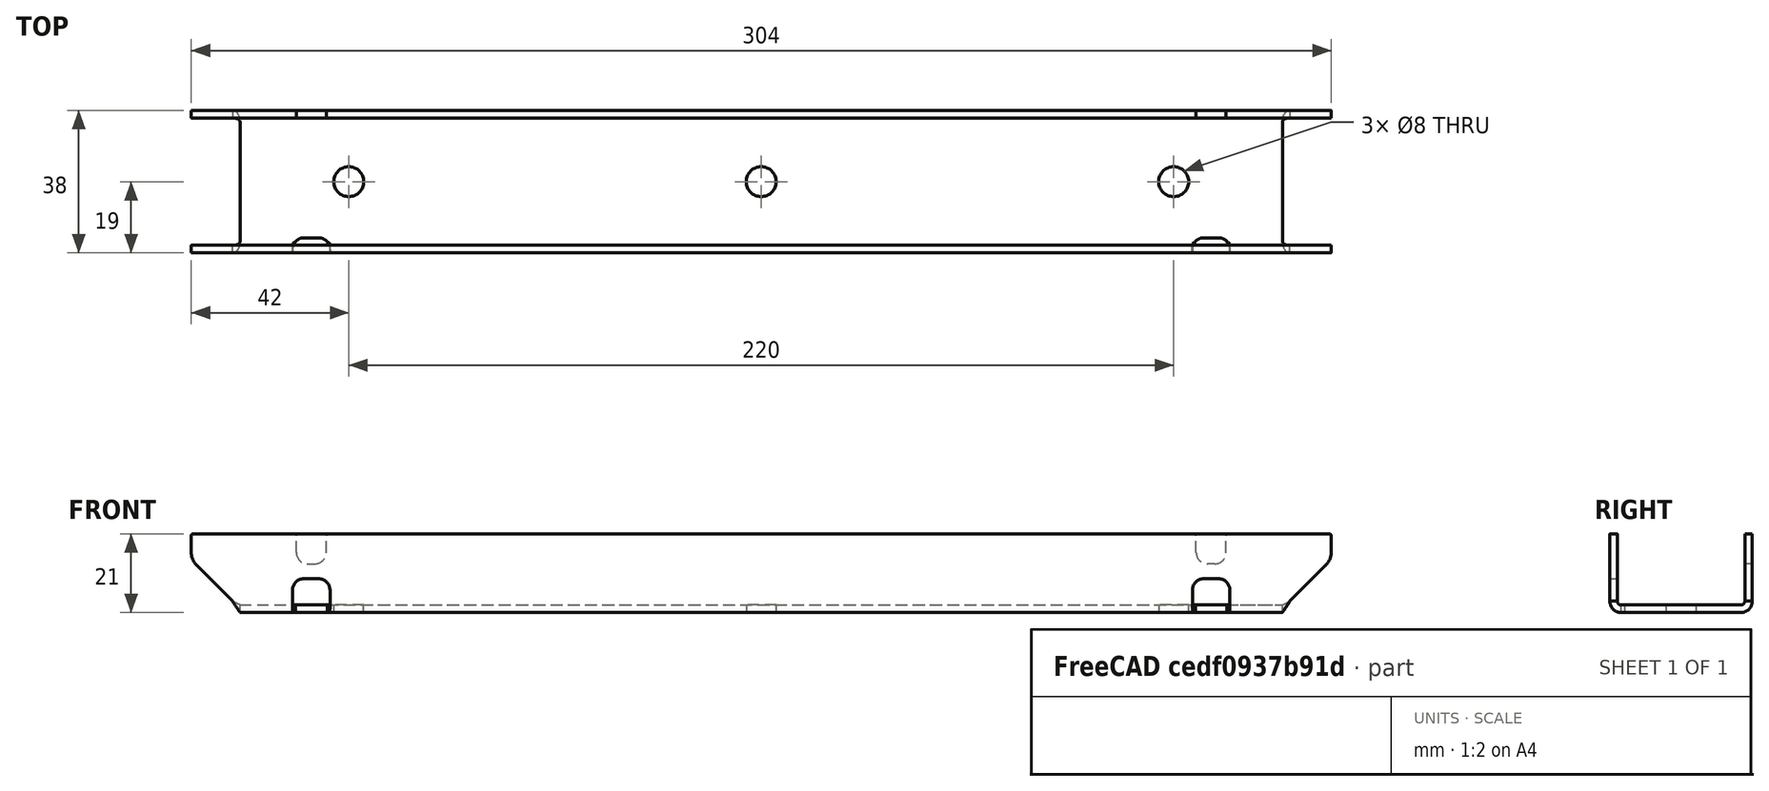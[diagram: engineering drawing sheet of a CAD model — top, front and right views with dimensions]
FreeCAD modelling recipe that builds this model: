
FCSTD DOCUMENT  (FreeCAD 0.19R18737 (Git))
Label: DXF-FILE-CONVERTED
License: All rights reserved
LicenseURL: http://en.wikipedia.org/wiki/All_rights_reserved
objects: Sketcher::SketchObject×3, PartDesign::FeaturePython×2, PartDesign::Pad×1, PartDesign::Body×1
note: 8 computed .brp shape members not serialized (recipe doc carries the construction recipe); baked Part::Feature solids carry a one-line shape summary decoded from their .brp

FEATURE [Sketcher::SketchObject] Sketch
  sketch-geometry (59):
    g0: LineSegment StartX=-152 StartY=-37.5 StartZ=0 EndX=-152 EndY=-33.0711 EndZ=0
    g1: LineSegment StartX=124.5 StartY=38 StartZ=0 EndX=151.5 EndY=38 EndZ=0
    g2: LineSegment StartX=-151.5 StartY=38 StartZ=0 EndX=-124.5 EndY=38 EndZ=0
    g3: LineSegment StartX=-115.5 StartY=38 StartZ=0 EndX=115.5 EndY=38 EndZ=0
    g4: LineSegment StartX=-151.5 StartY=-38 StartZ=0 EndX=151.5 EndY=-38 EndZ=0
    g5: LineSegment StartX=152 StartY=-37.5 StartZ=0 EndX=152 EndY=-33.0711 EndZ=0
    g6: LineSegment StartX=139 StartY=-17.7929 StartZ=0 EndX=139 EndY=17.7929 EndZ=0
    g7: LineSegment StartX=139.146 StartY=18.1464 StartZ=0 EndX=150.536 EndY=29.5355 EndZ=0
    g8: LineSegment StartX=139.146 StartY=-18.1464 StartZ=0 EndX=150.536 EndY=-29.5355 EndZ=0
    g9: LineSegment StartX=-139.146 StartY=18.1464 StartZ=0 EndX=-150.536 EndY=29.5355 EndZ=0
    g10: LineSegment StartX=-139.146 StartY=-18.1464 StartZ=0 EndX=-150.536 EndY=-29.5355 EndZ=0
    g11: LineSegment StartX=-152 StartY=33.0711 StartZ=0 EndX=-152 EndY=37.5 EndZ=0
    g12: LineSegment StartX=152 StartY=33.0711 StartZ=0 EndX=152 EndY=37.5 EndZ=0
    g13: LineSegment StartX=-139 StartY=17.7929 StartZ=0 EndX=-139 EndY=-17.7929 EndZ=0
    g14: LineSegment StartX=-121 StartY=30 StartZ=0 EndX=-119 EndY=30 EndZ=0
    g15: LineSegment StartX=121 StartY=30 StartZ=0 EndX=119 EndY=30 EndZ=0
    g16: LineSegment StartX=-124 StartY=33 StartZ=0 EndX=-124 EndY=37.5 EndZ=0
    g17: LineSegment StartX=124 StartY=33 StartZ=0 EndX=124 EndY=37.5 EndZ=0
    g18: LineSegment StartX=-116 StartY=33 StartZ=0 EndX=-116 EndY=37.5 EndZ=0
    g19: LineSegment StartX=116 StartY=33 StartZ=0 EndX=116 EndY=37.5 EndZ=0
    g20: LineSegment StartX=-122 StartY=-26 StartZ=0 EndX=-118 EndY=-26 EndZ=0
    g21: LineSegment StartX=122 StartY=-26 StartZ=0 EndX=118 EndY=-26 EndZ=0
    g22: LineSegment StartX=-122 StartY=-15 StartZ=0 EndX=-118 EndY=-15 EndZ=0
    g23: LineSegment StartX=122 StartY=-15 StartZ=0 EndX=118 EndY=-15 EndZ=0
    g24: LineSegment StartX=-125 StartY=-23 StartZ=0 EndX=-125 EndY=-18 EndZ=0
    g25: LineSegment StartX=125 StartY=-23 StartZ=0 EndX=125 EndY=-18 EndZ=0
    g26: LineSegment StartX=-115 StartY=-23 StartZ=0 EndX=-115 EndY=-18 EndZ=0
    g27: LineSegment StartX=115 StartY=-23 StartZ=0 EndX=115 EndY=-18 EndZ=0
    g28: ArcOfCircle CenterX=139.5 CenterY=17.7929 CenterZ=0 NormalX=0 NormalY=0 NormalZ=1 AngleXU=0 Radius=0.5 StartAngle=2.35619 EndAngle=3.14159
    g29: ArcOfCircle CenterX=151.5 CenterY=37.5 CenterZ=0 NormalX=0 NormalY=0 NormalZ=1 AngleXU=0 Radius=0.5 StartAngle=0 EndAngle=1.5708
    g30: ArcOfCircle CenterX=139.5 CenterY=-17.7929 CenterZ=0 NormalX=0 NormalY=0 NormalZ=1 AngleXU=0 Radius=0.5 StartAngle=3.14159 EndAngle=3.92699
    g31: ArcOfCircle CenterX=151.5 CenterY=-37.5 CenterZ=0 NormalX=0 NormalY=0 NormalZ=1 AngleXU=0 Radius=0.5 StartAngle=4.71239 EndAngle=6.28319
    g32: ArcOfCircle CenterX=-151.5 CenterY=37.5 CenterZ=0 NormalX=0 NormalY=0 NormalZ=1 AngleXU=0 Radius=0.5 StartAngle=1.5708 EndAngle=3.14159
    g33: ArcOfCircle CenterX=-139.5 CenterY=17.7929 CenterZ=0 NormalX=0 NormalY=0 NormalZ=1 AngleXU=0 Radius=0.5 StartAngle=0 EndAngle=0.785398
    g34: ArcOfCircle CenterX=-139.5 CenterY=-17.7929 CenterZ=0 NormalX=0 NormalY=0 NormalZ=1 AngleXU=0 Radius=0.5 StartAngle=5.49779 EndAngle=6.28319
    g35: ArcOfCircle CenterX=-151.5 CenterY=-37.5 CenterZ=0 NormalX=0 NormalY=0 NormalZ=1 AngleXU=0 Radius=0.5 StartAngle=3.14159 EndAngle=4.71239
    g36: ArcOfCircle CenterX=-147 CenterY=33.0711 CenterZ=0 NormalX=0 NormalY=0 NormalZ=1 AngleXU=0 Radius=5 StartAngle=3.14159 EndAngle=3.92699
    g37: ArcOfCircle CenterX=-147 CenterY=-33.0711 CenterZ=0 NormalX=0 NormalY=0 NormalZ=1 AngleXU=0 Radius=5 StartAngle=2.35619 EndAngle=3.14159
    g38: ArcOfCircle CenterX=147 CenterY=33.0711 CenterZ=0 NormalX=0 NormalY=0 NormalZ=1 AngleXU=0 Radius=5 StartAngle=5.49779 EndAngle=6.28319
    g39: ArcOfCircle CenterX=147 CenterY=-33.0711 CenterZ=0 NormalX=0 NormalY=0 NormalZ=1 AngleXU=0 Radius=5 StartAngle=0 EndAngle=0.785398
    g40: ArcOfCircle CenterX=-119 CenterY=33 CenterZ=0 NormalX=0 NormalY=0 NormalZ=1 AngleXU=0 Radius=3 StartAngle=4.71239 EndAngle=6.28319
    g41: ArcOfCircle CenterX=119 CenterY=33 CenterZ=0 NormalX=0 NormalY=0 NormalZ=1 AngleXU=0 Radius=3 StartAngle=3.14159 EndAngle=4.71239
    g42: ArcOfCircle CenterX=-121 CenterY=33 CenterZ=0 NormalX=0 NormalY=0 NormalZ=1 AngleXU=0 Radius=3 StartAngle=3.14159 EndAngle=4.71239
    g43: ArcOfCircle CenterX=121 CenterY=33 CenterZ=0 NormalX=0 NormalY=0 NormalZ=1 AngleXU=0 Radius=3 StartAngle=4.71239 EndAngle=6.28319
    g44: ArcOfCircle CenterX=-118 CenterY=-18 CenterZ=0 NormalX=0 NormalY=0 NormalZ=1 AngleXU=0 Radius=3 StartAngle=0 EndAngle=1.5708
    g45: ArcOfCircle CenterX=118 CenterY=-18 CenterZ=0 NormalX=0 NormalY=0 NormalZ=1 AngleXU=0 Radius=3 StartAngle=1.5708 EndAngle=3.14159
    g46: ArcOfCircle CenterX=-122 CenterY=-18 CenterZ=0 NormalX=0 NormalY=0 NormalZ=1 AngleXU=0 Radius=3 StartAngle=1.5708 EndAngle=3.14159
    g47: ArcOfCircle CenterX=122 CenterY=-18 CenterZ=0 NormalX=0 NormalY=0 NormalZ=1 AngleXU=0 Radius=3 StartAngle=0 EndAngle=1.5708
    g48: ArcOfCircle CenterX=-122 CenterY=-23 CenterZ=0 NormalX=0 NormalY=0 NormalZ=1 AngleXU=0 Radius=3 StartAngle=3.14159 EndAngle=4.71239
    g49: ArcOfCircle CenterX=122 CenterY=-23 CenterZ=0 NormalX=0 NormalY=0 NormalZ=1 AngleXU=0 Radius=3 StartAngle=4.71239 EndAngle=6.28319
    g50: ArcOfCircle CenterX=-118 CenterY=-23 CenterZ=0 NormalX=0 NormalY=0 NormalZ=1 AngleXU=0 Radius=3 StartAngle=4.71239 EndAngle=6.28319
    g51: ArcOfCircle CenterX=118 CenterY=-23 CenterZ=0 NormalX=0 NormalY=0 NormalZ=1 AngleXU=0 Radius=3 StartAngle=3.14159 EndAngle=4.71239
    g52: ArcOfCircle CenterX=-115.5 CenterY=37.5 CenterZ=0 NormalX=0 NormalY=0 NormalZ=1 AngleXU=0 Radius=0.5 StartAngle=1.5708 EndAngle=3.14159
    g53: ArcOfCircle CenterX=-124.5 CenterY=37.5 CenterZ=0 NormalX=0 NormalY=0 NormalZ=1 AngleXU=0 Radius=0.5 StartAngle=0 EndAngle=1.5708
    g54: ArcOfCircle CenterX=124.5 CenterY=37.5 CenterZ=0 NormalX=0 NormalY=0 NormalZ=1 AngleXU=0 Radius=0.5 StartAngle=1.5708 EndAngle=3.14159
    g55: ArcOfCircle CenterX=115.5 CenterY=37.5 CenterZ=0 NormalX=0 NormalY=0 NormalZ=1 AngleXU=0 Radius=0.5 StartAngle=0 EndAngle=1.5708
    g56: Circle CenterX=-110 CenterY=-6.7e-15 CenterZ=0 NormalX=0 NormalY=0 NormalZ=1 AngleXU=0 Radius=4
    g57: Circle CenterX=110 CenterY=6.7e-15 CenterZ=0 NormalX=0 NormalY=0 NormalZ=1 AngleXU=0 Radius=4
    g58: Circle CenterX=0 CenterY=0 CenterZ=0 NormalX=0 NormalY=0 NormalZ=1 AngleXU=0 Radius=4
  constraints (56):
    c: Coincident(g0,g35)
    c: Coincident(g0,g37)
    c: Coincident(g36,g11)
    c: Coincident(g11,g32)
    c: Coincident(g4,g35)
    c: Coincident(g2,g32)
    c: Coincident(g10,g37)
    c: Coincident(g36,g9)
    c: Coincident(g34,g10)
    c: Coincident(g9,g33)
    c: Coincident(g34,g13)
    c: Coincident(g13,g33)
    c: Coincident(g48,g24)
    c: Coincident(g24,g46)
    c: Coincident(g2,g53)
    c: Coincident(g42,g16)
    c: Coincident(g16,g53)
    c: Coincident(g20,g48)
    c: Coincident(g22,g46)
    c: Coincident(g14,g42)
    c: Coincident(g14,g40)
    c: Coincident(g20,g50)
    c: Coincident(g44,g22)
    c: Coincident(g40,g18)
    c: Coincident(g18,g52)
    c: Coincident(g3,g52)
    c: Coincident(g50,g26)
    c: Coincident(g44,g26)
    c: Coincident(g27,g51)
    c: Coincident(g27,g45)
    c: Coincident(g55,g3)
    c: Coincident(g19,g41)
    c: Coincident(g19,g55)
    c: Coincident(g21,g51)
    c: Coincident(g45,g23)
    c: Coincident(g15,g41)
    c: Coincident(g43,g15)
    c: Coincident(g49,g21)
    c: Coincident(g47,g23)
    c: Coincident(g17,g43)
    c: Coincident(g17,g54)
    c: Coincident(g54,g1)
    c: Coincident(g25,g49)
    c: Coincident(g25,g47)
    c: Coincident(g6,g30)
    c: Coincident(g6,g28)
    c: Coincident(g8,g30)
    c: Coincident(g7,g28)
    c: Coincident(g8,g39)
    c: Coincident(g7,g38)
    c: Coincident(g4,g31)
    c: Coincident(g1,g29)
    c: Coincident(g31,g5)
    c: Coincident(g5,g39)
    c: Coincident(g12,g38)
    c: Coincident(g12,g29)
FEATURE [PartDesign::Pad] Pad
  Length = 2
  Length2 = 100
  Profile = -> Sketch
  Refine = true
  Type = 0
FEATURE [Sketcher::SketchObject] Sketch001
  ExternalGeometry = -> [Pad]
  MapMode = 5
  Placement = pos=(0,0,2) rot=(0,0,1;0rad)
  Support = -> [Pad]
  sketch-geometry (1):
    g0: LineSegment StartX=-153.372 StartY=18 StartZ=0 EndX=151.701 EndY=18 EndZ=0
  constraints (2):
    c: Horizontal(g0)
    c: DistanceY(g0,g-3) = 20
FEATURE [Sketcher::SketchObject] Sketch002
  MapMode = 5
  Placement = pos=(0,0,2) rot=(0,0,1;0rad)
  sketch-geometry (1):
    g0: LineSegment StartX=-167.86 StartY=-18 StartZ=0 EndX=155.964 EndY=-18 EndZ=0
  constraints (1):
    c: Horizontal(g0)
FEATURE [PartDesign::FeaturePython] Fold  # WARN: FeaturePython — macro-defined, semantics opaque (R4)
  BaseFeature = -> Pad
  BendLine = -> Sketch002
  angle = 90
  baseObject = -> Pad [Face61]
  invert = false
  invertbend = true
  kfactor = 0.5
  radius = 1
  unfold = false
FEATURE [PartDesign::FeaturePython] Fold001  # WARN: FeaturePython — macro-defined, semantics opaque (R4)
  BaseFeature = -> Fold
  BendLine = -> Sketch001
  angle = 90
  baseObject = -> Fold [Face18]
  invert = false
  invertbend = false
  kfactor = 0.5
  radius = 1
  unfold = false
FEATURE [PartDesign::Body] Body
  Group = -> [Pad,Sketch001,Sketch002,Fold,Fold001]
  Origin = -> Origin
  Tip = -> Fold001
